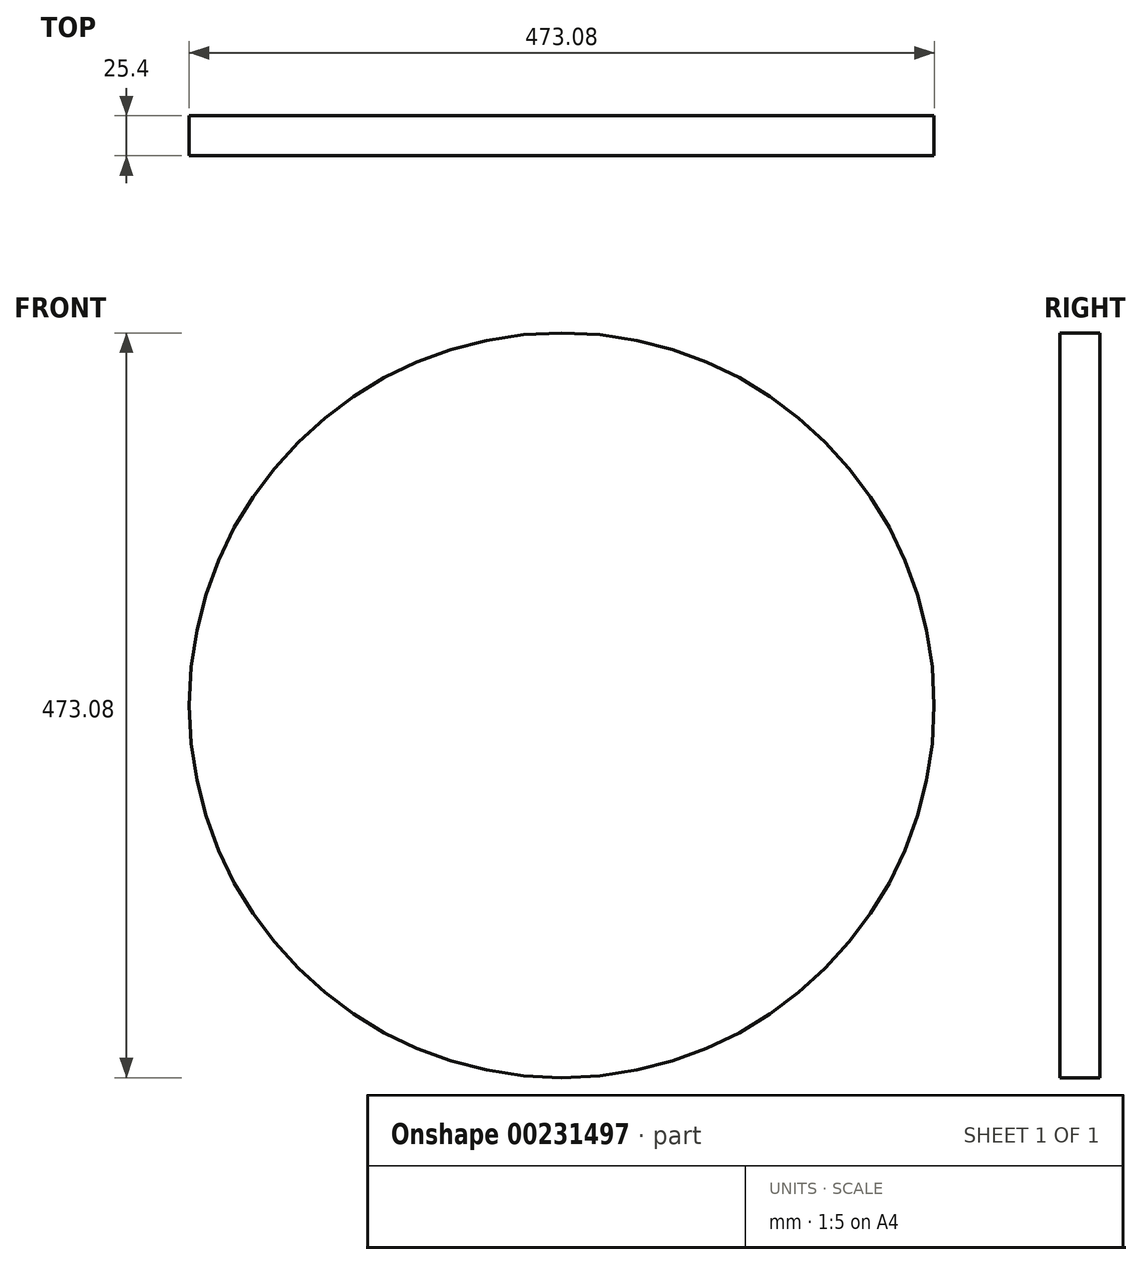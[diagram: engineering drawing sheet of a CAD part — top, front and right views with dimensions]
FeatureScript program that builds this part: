
annotation { "Feature Type Name" : "Feature", "Feature Type Description" : "" }
export const myFeature = defineFeature(function(context is Context, id is Id, definition is map)
    precondition{}
    {
        {
            var Q0;
            Q0=qCreatedBy(makeId("Front.planeOp"),FACE);
            var sketch = newSketch(context, id + "F0", { "sketchPlane" : qUnion([Q0])});
            skCircle(sketch, "E0", {"center": v(0, 0) * mm, "radius": 236.54 * mm});
            skSolve(sketch);
        }
        {
            var Q0;
            Q0 = qSketchRegion(id + "F0", true);
            extrude(context, id + "F1", {"entities" : qUnion([Q0]), "depth" : 25.4 * mm});
        }
    });
